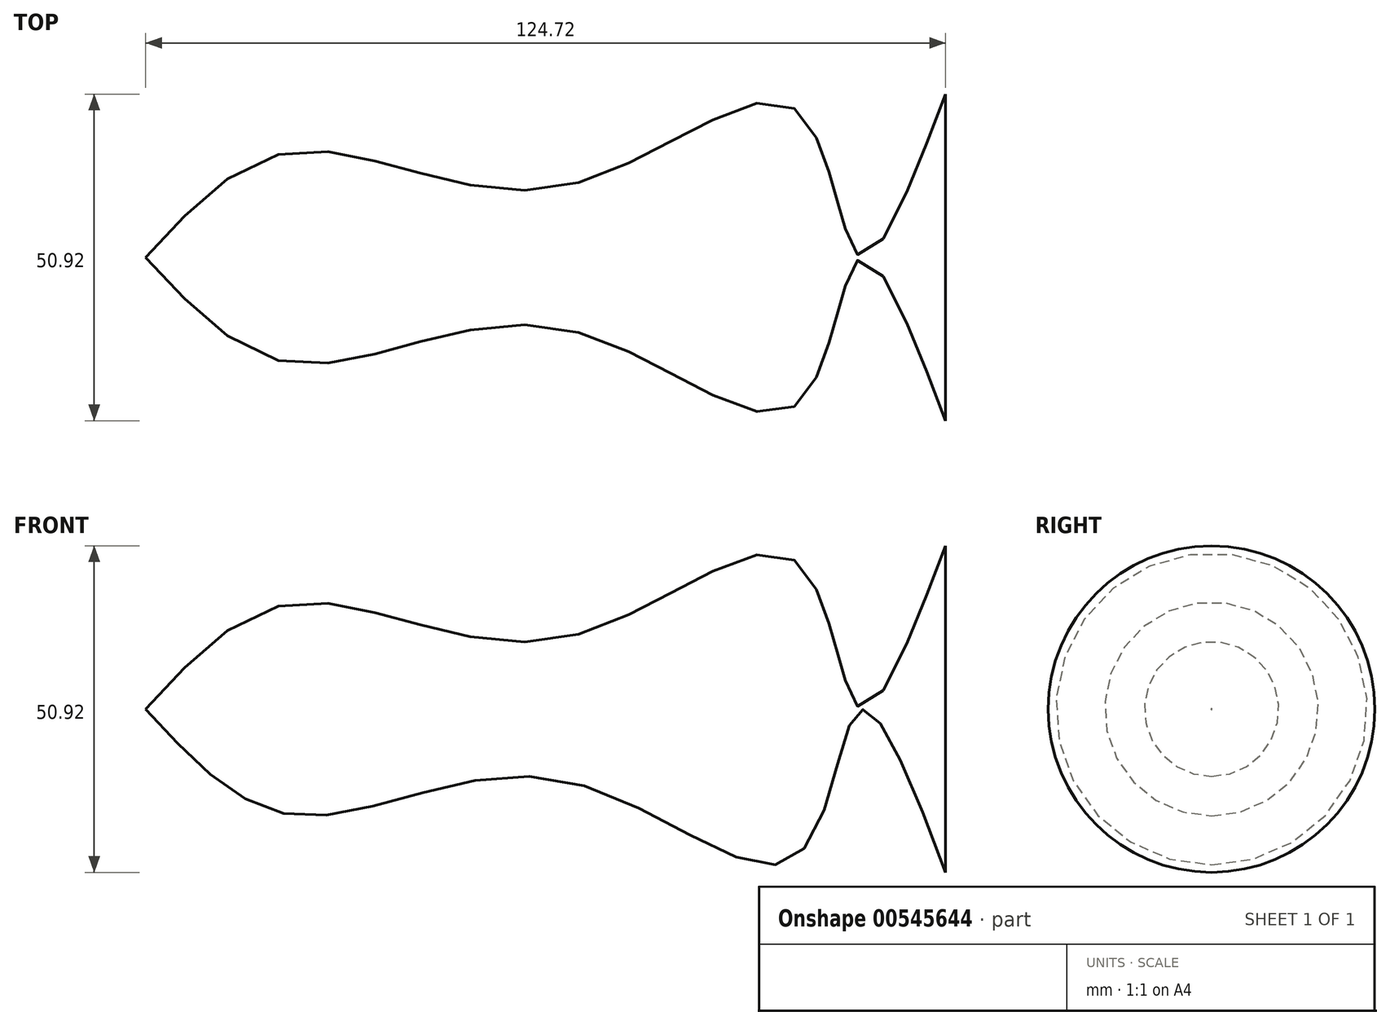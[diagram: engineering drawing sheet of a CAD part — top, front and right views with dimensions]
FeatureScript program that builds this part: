
annotation { "Feature Type Name" : "Feature", "Feature Type Description" : "" }
export const myFeature = defineFeature(function(context is Context, id is Id, definition is map)
    precondition{}
    {
        {
            var Q0;
            Q0=qCreatedBy(makeId("Front.planeOp"),FACE);
            var sketch = newSketch(context, id + "F0", { "sketchPlane" : qUnion([Q0])});
            skFitSpline(sketch, "E0", {"points": [v(-58.87, -4.58) * mm, v(-34.89, -21.18) * mm, v(6.07, -15.65) * mm, v(42.23, -27.82) * mm, v(52.2, -4.95) * mm, v(65.85, -30.04) * mm], "startDerivative": vector(113.63, -125.04) * mm, "endDerivative": vector(83.5, -219.44) * mm});
            skLineSegment(sketch, "E1", {"start": v(-58.87, -4.58) * mm, "end": v(65.85, -4.58) * mm});
            skLineSegment(sketch, "E2", {"start": v(65.85, -4.58) * mm, "end": v(65.85, -30.04) * mm});
            skSolve(sketch);
        }
        {
            var Q0;
            Q0 = qSketchRegion(id + "F0", true);
            var Q1;
            Q1=sQuery(id+"F0.wireOp",EDGE,"E1");
            revolve(context, id + "F1", {"entities" : qUnion([Q0]), "axis" : qUnion([Q1]), "revolveType" : RevolveType.FULL});
        }
    });
